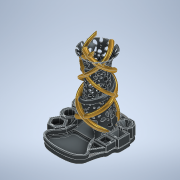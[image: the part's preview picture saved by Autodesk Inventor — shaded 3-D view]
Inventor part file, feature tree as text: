
AUTODESK INVENTOR PART (.ipt)
format: ipt  version: 2022 (Build 260153000, 153)  size: 10,258,432 bytes
history: native  units: mm
features: sketch x29, extrude x25, fillet x12, helix x5, plane x3, chamfer x3, revolve x2, pattern_circular x2
ambient origin geometry x8: Origin, YZ Plane, XZ Plane, XY Plane, X Axis, Y Axis, Z Axis, Center Point
bodies: Solid1 (feature_tree)
feature tree (81):
  revolve  "Revolution1"  [1 undecoded]
  plane  "Work Plane1"
  extrude  "Extrusion4"  Depth=20.0mm
  extrude  "Extrusion2"  Depth=19.0mm
  pattern_circular  "Circular Pattern2"  Count=11  [1 undecoded]
  plane  "Work Plane3"
  extrude  "Extrusion3"  Depth=10.0mm
  pattern_circular  "Circular Pattern3"  Count=7  [1 undecoded]
  helix  "Coil1"  [1 undecoded]
  helix  "Coil2"  [1 undecoded]
  helix  "Coil3"  [1 undecoded]
  helix  "Coil4"  [1 undecoded]
  helix  "Coil5"  [1 undecoded]
  extrude  "Extrusion5"  Depth=20.0mm
  revolve  "Revolution2"  [1 undecoded]
  extrude  "Extrusion6"  Depth=30.0mm
  extrude  "Extrusion7"  Depth=15.0mm
  extrude  "Extrusion15"  Depth=30.0mm
  extrude  "Extrusion16"  Depth=45.0mm
  extrude  "Extrusion17"  Depth=13.0mm
  extrude  "Extrusion18"  Depth=39.0mm
  extrude  "Extrusion19"  Depth=11.0mm
  extrude  "Extrusion20"  Depth=10.0mm
  extrude  "Extrusion21"  Depth=11.0mm
  extrude  "Extrusion22"  Depth=9.0mm
  extrude  "Extrusion23"  Depth=3.0mm TaperAngle=0.0deg
  extrude  "Extrusion25"  Depth=43.0mm
  fillet  "Fillet3"  [1 undecoded]
  extrude  "Extrusion26"  Depth=54.0mm TaperAngle=0.0deg
  extrude  "Extrusion27"  Depth=35.0mm
  extrude  "Extrusion28"  Depth=30.0mm
  extrude  "Extrusion29"  Depth=30.0mm
  extrude  "Extrusion30"  Depth=35.0mm
  extrude  "Extrusion31"  Depth=35.0mm
  extrude  "Extrusion32"  Depth=5.0mm
  chamfer  "Chamfer1"  Distance=10.0mm
  extrude  "Extrusion33"  Depth=5.0mm TaperAngle=0.0deg
  chamfer  "Chamfer2"  Distance=10.0mm
  chamfer  "Chamfer3"  Distance=15.0mm
  fillet  "Fillet4"  Radius=0.2mm
  fillet  "Fillet5"  Radius=5.0mm
  fillet  "Fillet6"  Radius=10.0mm
  fillet  "Fillet7"  Radius=15.0mm
  fillet  "Fillet8"  Radius=10.0mm
  fillet  "Fillet9"  Radius=7.0mm
  fillet  "Fillet10"  Radius=3.6mm
  fillet  "Fillet11"  Radius=10.0mm
  fillet  "Fillet12"  Radius=20.0mm
  fillet  "Fillet13"  Radius=24.0mm
  fillet  "Fillet14"  Radius=20.0mm
  extrude  "Extrusion34"  Depth=30.0mm
  sketch  "Sketch1"  dims[d11=60.0mm d12=40.0mm]
  sketch  "Sketch3"  dims[d13=20.0mm d14=20.0mm]
  plane  "Work Plane2"
  sketch  "Sketch4"  dims[d15=20.0mm d16=19.0mm d17=110.0mm]
  sketch  "Sketch5"  dims[d18=40.0mm d19=10.0mm]
  sketch  "Sketch7"  dims[d20=179.0mm]
  sketch  "Sketch8"  dims[d26=2.0mm]
  sketch  "Sketch9"  dims[d27=2.0mm]
  sketch  "Sketch10"  dims[d28=2.0mm]
  sketch  "Sketch11"  dims[d29=2.0mm]
  sketch  "Sketch13"  dims[d30=2.0mm]
  sketch  "Sketch16"  dims[d31=90.0deg d32=70.0mm d38=77.75mm d39=0.0mm d40=40.0mm d41=360.0deg d43=70.0mm d44=77.75mm d45=0.0mm d46=40.0mm d47=360.0deg]
  sketch  "Sketch17"  dims[d49=20.0mm d50=20.0mm]
  sketch  "Sketch20"  dims[d51=20.0mm d52=20.0mm]
  sketch  "Sketch21"  dims[d53=40.0mm d54=30.0mm]
  sketch  "Sketch22"  dims[d55=30.0mm d56=15.0mm]
  sketch  "Sketch23"  dims[d57=15.0mm d58=30.0mm]
  sketch  "Sketch26"  dims[d59=77.75mm d60=0.0mm d61=45.0mm]
  sketch  "Sketch27"  dims[d62=35.0mm]
  sketch  "Sketch28"  dims[d63=70.0mm d64=120.0mm d65=10.0mm d66=-0.567232mm d67=90.0deg d68=90.0deg d69=90.0deg d70=90.0deg d71=13.0mm]
  sketch  "Sketch30"  dims[d72=10.0mm d73=39.0mm]
  sketch  "Sketch31"  dims[d74=140.0mm d75=180.0mm d76=10.0mm d77=-0.645772mm d78=90.0deg d79=90.0deg d80=90.0deg d81=90.0deg d82=11.0mm]
  sketch  "Sketch33"  dims[d83=39.0mm d84=10.0mm]
  sketch  "Sketch35"  dims[d85=135.0mm d86=180.0mm d87=10.0mm d88=-0.645772mm d89=90.0deg d90=90.0deg d91=90.0deg d92=90.0deg d93=11.0mm]
  sketch  "Sketch37"  dims[d94=170.0mm d95=190.0mm d96=10.0mm d97=-0.645772mm d98=90.0deg d99=90.0deg d100=90.0deg d101=90.0deg d102=9.0mm]
  sketch  "Sketch38"  dims[d103=170.0mm d104=190.0mm d105=10.0mm d106=-0.645772mm d107=90.0deg d108=90.0deg d109=90.0deg d110=90.0deg d125=3.0mm d126=0.0mm]
  sketch  "Sketch39"  dims[d128=60.0mm d129=43.0mm d130=270.0deg]
  sketch  "Sketch40"  dims[d132=34.0mm d133=54.0mm d134=0.0mm]
  sketch  "Sketch41"  dims[d136=54.0mm d137=0.0mm d141=35.0mm]
  sketch  "Sketch43"  dims[d165=35.0mm d166=30.0mm d167=30.0mm d168=30.0mm d169=30.0mm d170=35.0mm d172=35.0mm d186=5.0mm d187=10.0mm d188=0.0mm d190=5.0mm d191=0.0mm d192=10.0mm d193=0.0mm d194=15.0mm d195=0.0mm d196=0.2mm d197=0.0mm d198=5.0mm d199=0.0mm d200=10.0mm d201=0.0mm d202=15.0mm d203=0.0mm d204=10.0mm d205=0.0mm d210=7.0mm d211=0.0mm d212=3.6mm d213=10.0mm d214=0.0mm d215=20.0mm d216=24.0mm d217=20.0mm d218=30.0mm d219=23.5mm d220=5.75mm d221=5.75mm d222=5.75mm d223=14.0mm d224=0.0mm d225=22.5mm d226=6.25mm d227=6.25mm d228=6.25mm d229=14.0mm d230=0.0mm d231=25.0mm d232=5.0mm d233=5.0mm d234=5.0mm d235=14.0mm d236=0.0mm d237=25.5mm d239=3.0mm d241=10.0mm d242=0.0mm d243=54.0mm d244=43.0mm d245=17.5mm d246=17.5mm d247=7.0mm d248=5.5mm d249=4.0mm d250=3.607976mm d251=10.0mm d252=0.0mm d253=21.0mm d254=21.0mm d255=5.0mm d256=4.0mm d257=5.0mm d258=24.0mm d259=0.0mm d260=10.0mm d261=2.0mm d262=45.0deg d263=25.0mm d266=5.0mm d267=5.0mm d268=12.0mm d269=0.0mm d270=11.0mm d271=2.0mm d272=45.0deg d273=12.0mm d274=2.0mm d275=45.0deg d276=35.0mm d277=3.0mm d278=5.0mm d279=5.0mm d280=5.0mm d281=2.0mm d282=2.0mm d283=1.56mm d284=1.0mm d285=1.0mm d286=1.0mm d287=1.0mm d288=1.0mm d289=1.0mm d290=1.0mm d291=1.0mm d292=20.0mm d293=0.0mm d135=0.0mm]
note: 10 required parameter values undecoded (feature->parameter linkage not recoverable at this tier; creation-order binding heuristic only, values carry confidence <= 0.55)